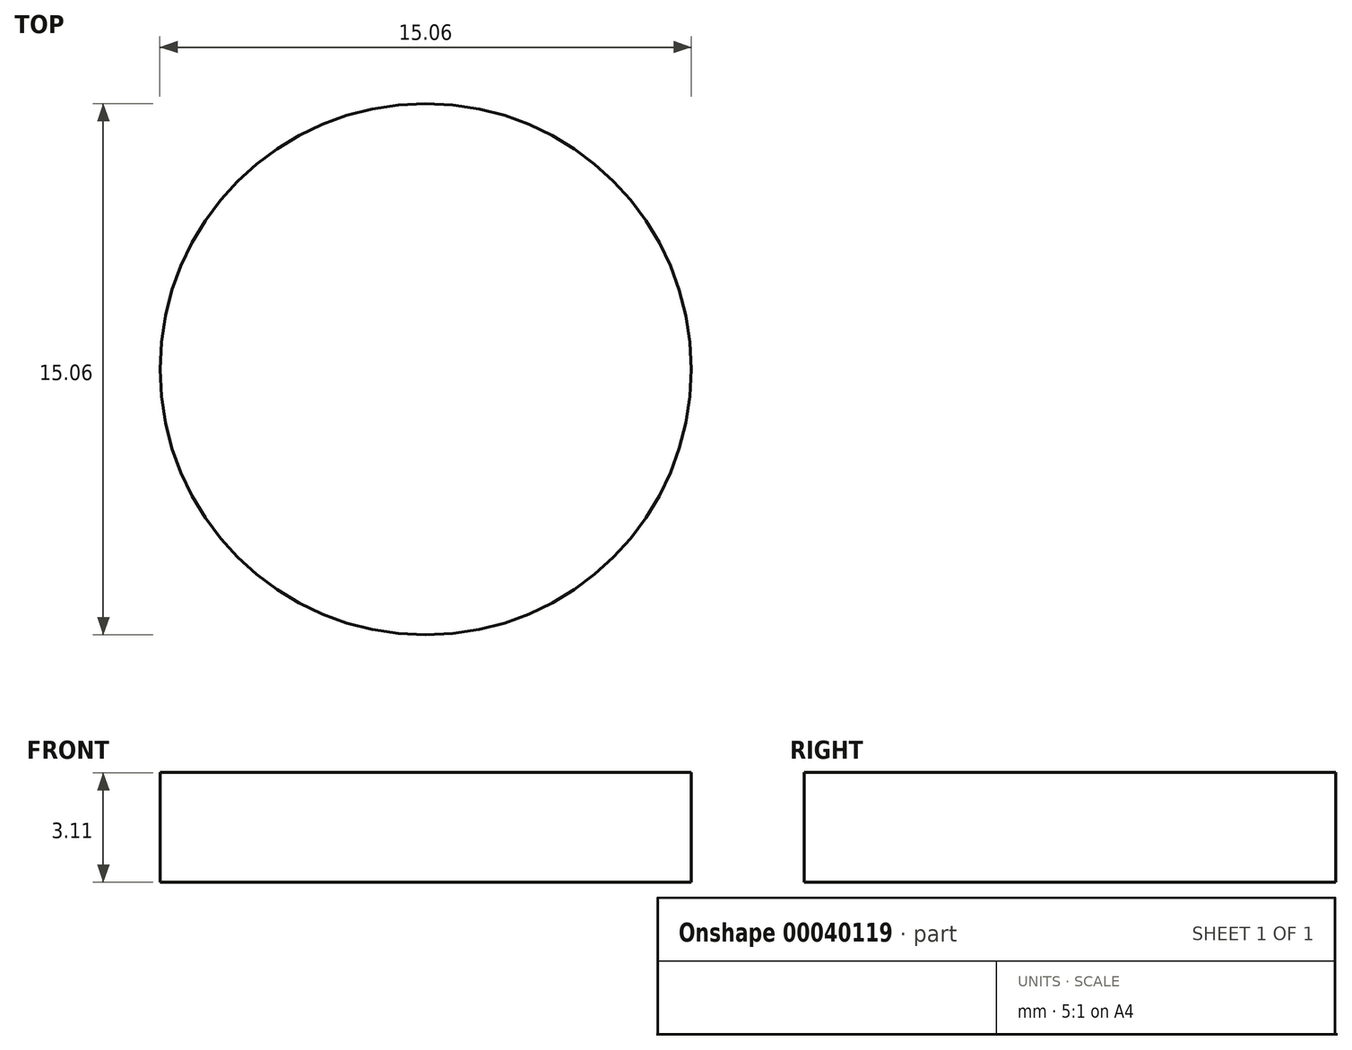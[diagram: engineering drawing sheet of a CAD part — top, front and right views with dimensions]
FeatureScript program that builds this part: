
annotation { "Feature Type Name" : "Feature", "Feature Type Description" : "" }
export const myFeature = defineFeature(function(context is Context, id is Id, definition is map)
    precondition{}
    {
        {
            var Q0;
            Q0=qCreatedBy(makeId("Top.planeOp"),FACE);
            var sketch = newSketch(context, id + "F0", { "sketchPlane" : qUnion([Q0])});
            skCircle(sketch, "E0", {"center": v(0, 0) * mm, "radius": 7.53 * mm});
            skSolve(sketch);
        }
        {
            var Q0;
            Q0=makeQuery(id+"F0.imprint","IMPRINT",FACE,{"disambiguationData":[TD([[makeQuery(id+"F0.imprint","IMPRINT",EDGE,{"derivedFrom":sQuery(id+"F0.wireOp",EDGE,"E0")}),1.0]])]});
            extrude(context, id + "F1", {"entities" : qUnion([Q0]), "depth" : 3.1 * mm});
        }
    });
